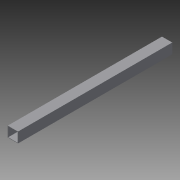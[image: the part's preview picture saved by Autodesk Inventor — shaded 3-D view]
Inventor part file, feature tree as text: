
AUTODESK INVENTOR PART (.ipt)
format: ipt  version: 2015 (Build 190159000, 159)  size: 89,600 bytes
history: native  units: in
note: dims shown in document units (in); Inventor stores cm internally (conversion verified against a paired STEP export)
features: extrude x2, sketch x2
ambient origin geometry x8: Origin, YZ Plane, XZ Plane, XY Plane, X Axis, Y Axis, Z Axis, Center Point
bodies: Solid1 (feature_tree)
feature tree (4):
  extrude  "Extrusion1"  Depth=2.0in
  extrude  "Extrusion2"  Depth=0.083in TaperAngle=0.0deg
  sketch  "Sketch1"  dims[d0=2.0in d1=2.0in]
  sketch  "Sketch2"  dims[d2=0.083in d3=33.0in d4=0.0in d7=165.0deg d9=30.0in d10=0.0in d11=165.0deg]
